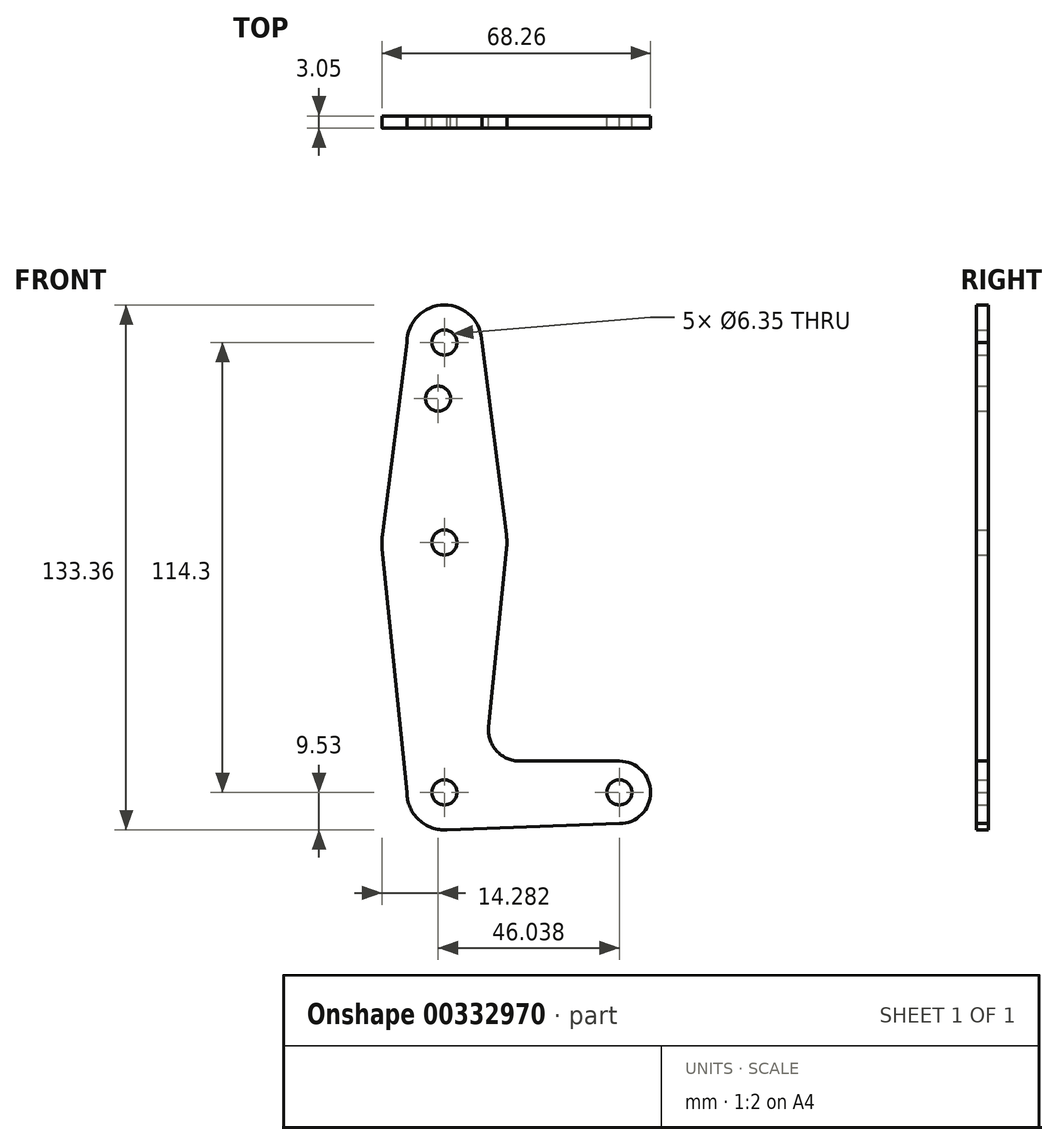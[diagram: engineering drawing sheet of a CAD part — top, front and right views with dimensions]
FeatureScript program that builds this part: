
annotation { "Feature Type Name" : "Feature", "Feature Type Description" : "" }
export const myFeature = defineFeature(function(context is Context, id is Id, definition is map)
    precondition{}
    {
        {
            var Q0;
            Q0=qCreatedBy(makeId("Front.planeOp"),FACE);
            var sketch = newSketch(context, id + "F0", { "sketchPlane" : qUnion([Q0])});
            skLineSegment(sketch, "E0", {"start": v(0, 114.3) * mm, "end": v(0, 0) * mm, "construction": true});
            skLineSegment(sketch, "E1", {"start": v(0, 0) * mm, "end": v(44.45, 0) * mm, "construction": true});
            skCircle(sketch, "E2", {"center": v(0, 114.3) * mm, "radius": 9.53 * mm});
            skCircle(sketch, "E3", {"center": v(0, 0) * mm, "radius": 9.53 * mm});
            skCircle(sketch, "E4", {"center": v(44.45, 0) * mm, "radius": 7.94 * mm});
            skCircle(sketch, "E5", {"center": v(0, 63.5) * mm, "radius": 15.88 * mm});
            skLineSegment(sketch, "E6", {"start": v(-9.53, 0) * mm, "end": v(-15.8, 61.9) * mm});
            skLineSegment(sketch, "E7", {"start": v(11.25, 16.68) * mm, "end": v(15.8, 61.9) * mm});
            skLineSegment(sketch, "E8", {"start": v(9.53, 114.3) * mm, "end": v(15.75, 65.5) * mm});
            skLineSegment(sketch, "E9", {"start": v(-9.53, 114.3) * mm, "end": v(-15.75, 65.5) * mm});
            skLineSegment(sketch, "E10", {"start": v(19.16, 7.94) * mm, "end": v(44.45, 7.94) * mm});
            skLineSegment(sketch, "E11", {"start": v(0, -9.52) * mm, "end": v(44.45, -7.94) * mm});
            skCircle(sketch, "E12", {"center": v(0, 114.3) * mm, "radius": 3.18 * mm});
            skCircle(sketch, "E13", {"center": v(0, 63.5) * mm, "radius": 3.18 * mm});
            skCircle(sketch, "E14", {"center": v(0, 0) * mm, "radius": 3.18 * mm});
            skCircle(sketch, "E15", {"center": v(44.45, 0) * mm, "radius": 3.18 * mm});
            skCircle(sketch, "E16", {"center": v(-1.59, 100.03) * mm, "radius": 3.18 * mm});
            skArc(sketch, "E17.filletArc", {"start": v(11.25, 16.68) * mm, "mid": v(13.26, 10.55) * mm, "end": v(19.16, 7.94) * mm});
            skSolve(sketch);
        }
        {
            var Q0;
            Q0 = qSketchRegion(id + "F0", true);
            extrude(context, id + "F1", {"entities" : qUnion([Q0]), "depth" : 3.05 * mm});
        }
    });
